# Revit family: 2069244 Sylvania Lighting Fixture OFFICELYTE 600 HE 4K DALI
name_source: partatom
category: Lighting Fixtures
revit_build: Autodesk Revit 2017 (Build: 20190507_1515(x64)
units: mm (PartAtom-declared; Revit-internal decimal feet)

## family parameters
Cut with Voids When Loaded = No
Host = Face
Light Source = Yes
OmniClass Number = 23.80.70.11.17
OmniClass Title = Specialized Lighting by Location or Use
Part Type = Normal
Room Calculation Point = No
Round Connector Dimension = Use Diameter
Shared = No

## types (1)
- 2069244 OFFICELYTE 600 HE 4K DALI
    Apparent Load = 24 VA
    Assembly Code = D5020200
    AssetType = Fixed
    Color Filter = 16777215
    Default Elevation = 0 mm  [stored 0 ft]
    Description = The Concord OFFICELYTE LP LED HO 4K 600 is a high efficient luminaire for Office, education, meeting rooms. With efficacy of 95lm/W, at 4549lm, CRI of 85 and a very low glare ratio according to EN12464.
    Dimming Lamp Color Temperature Shift = <None>
    DimmingControlOptions = Dimmable
    DocumentationLiterature = http://www.sylvania-lighting.com
    DurationUnit = hours
    ElectricShockClassification = Class I
    Emit Shape Visible in Rendering = No
    Emit from Rectangle Length = 564 mm
    Emit from Rectangle Width = 564 mm
    ExpectedLife = 50000
    Height_SYL = 84 mm
    IfcExportAs = IfcLightFixtureType
    IfcExportType = IfcLightFixtureType
    ImpactProtectionIndex = IK02
    IngressProtection = IP20
    InputNominalFrequency = 50/60 Hz
    InputVoltage = 230-240V~
    Keynote = 16500
    Lamp = LED
    LampColourRenderingIndex = 80
    LampColourTemperature = 4000 K
    LampNominalLuminous = 3545 lm
    LampsType = LED
    Length_SYL = 595 mm  [stored 1.9521 ft]
    LightOutputRatio = 100
    LuminousEfficacy = 148 lm/W
    Manufacturer = Havells-Sylvania Group
    ManufacturerName = Feilo Sylvania
    Material = zintec housing, acrylic diffuser
    Material_1_SYL = Steel_Sylvania_Officelyte LP LED_White_RAL 9016
    Material_2_SYL = Acrylic_Sylvania_Officelyte LP LED_Satin_4000K
    Material_3_SYL = Steel_Sylvania_Officelyte LP LED_White_RAL 9016
    Model = OFFICELYTE 600 HE 4K DALI
    ModelNumber = 2069244
    ModelReference = OFFICELYTE 600 HE 4K DALI
    Name = OFFICELYTE 600 HE 4K DALI
    NominalHeight = 87 mm
    NominalLength = 595 mm  [stored 1.9521 ft]
    NominalWidth = 0 mm  [stored 0 ft]
    Photometric Web File = 2069244.ies
    PowerConsumption = 24 W
    PowerFactor = 0.96
    Tilt Angle = -90.00°
    TypeName = OFFICELYTE 600 HE 4K DALI
    URL = http://www.sylvania-lighting.com
    Voltage = 230 V
    Weight = 6.0 kg
    Width_SYL = 595 mm  [stored 1.9521 ft]

note: [stored X ft] marks values corroborated as IEEE doubles in the binary element streams (Revit-internal decimal feet)

## geometry (parser evidence)
native form markers: Sweep x3
no freeform markers — native parametric forms only
